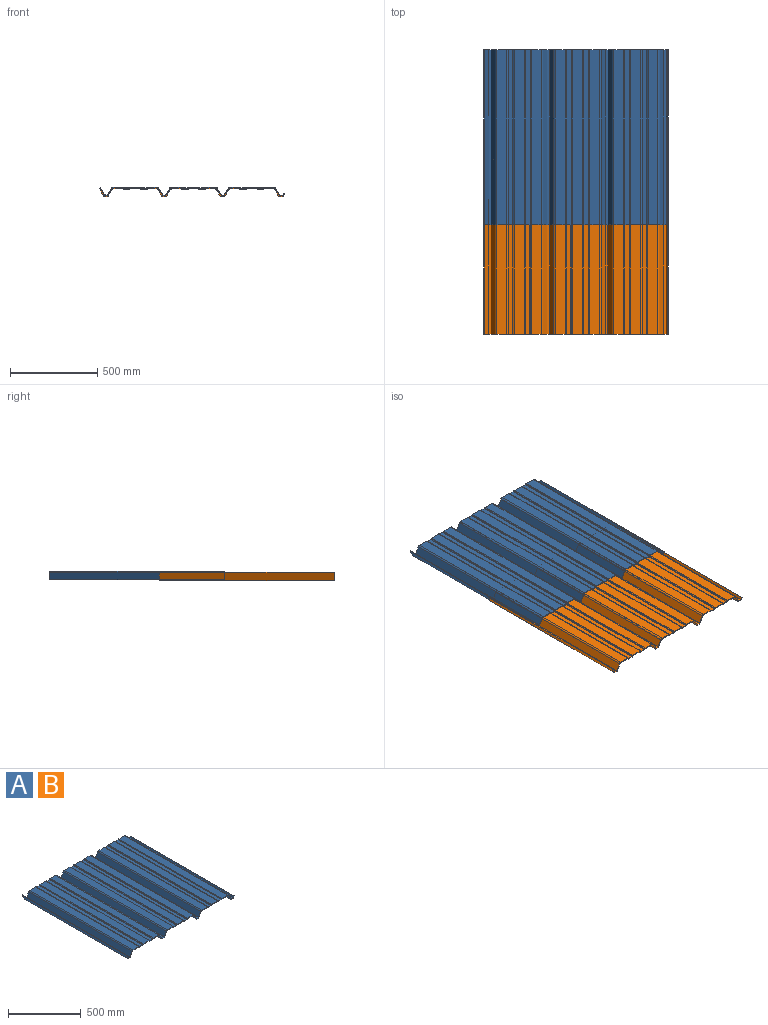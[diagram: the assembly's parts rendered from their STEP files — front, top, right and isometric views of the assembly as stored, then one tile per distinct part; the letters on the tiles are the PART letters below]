
ASSEMBLY  parts=2 mates=1
PART A: 157 faces, bbox 1056.4x1000x50 mm
  f0: plane 1000x41mm, normal (-0.87,0,-0.5), area 47365.7mm2, adj f1,f154,f155,f156
  f1: cylinder r=6mm len=1000mm, axis (0,1,0), area 6279mm2, adj f0,f2,f155,f156
  f2: plane 1000x15.07mm, normal (0,0,-1), area 15074.6mm2, adj f1,f3,f155,f156
  f3: cylinder r=6mm len=1000mm, axis (0,1,0), area 6283.2mm2, adj f2,f4,f155,f156
  f4: plane 1000x38mm, normal (0.87,0,-0.5), area 43878.6mm2, adj f3,f5,f155,f156
  f5: cylinder r=6mm len=1000mm, axis (0,1,0), area 6283.2mm2, adj f4,f6,f155,f156
  f6: plane 1000x57.03mm, normal (0,0,-1), area 57032.5mm2, adj f5,f7,f155,f156
  f7: cylinder r=1.7mm len=1000mm, axis (0,1,0), area 1276.9mm2, adj f6,f8,f155,f156
  f8: plane 1000x3.84mm, normal (-0.68,0,-0.73), area 5253.3mm2, adj f7,f9,f155,f156
  f9: cylinder r=1.7mm len=1000mm, axis (0,1,0), area 1276.9mm2, adj f8,f10,f155,f156
  f10: plane 1000x28.68mm, normal (0,0,-1), area 28679.7mm2, adj f9,f11,f155,f156
  f11: cylinder r=1.7mm len=1000mm, axis (0,1,0), area 1276.9mm2, adj f10,f12,f155,f156
  f12: plane 1000x3.84mm, normal (0.68,0,-0.73), area 5253.4mm2, adj f11,f13,f155,f156
  f13: cylinder r=1.7mm len=1000mm, axis (0,1,0), area 1276.9mm2, adj f12,f14,f155,f156
  f14: plane 1000x58mm, normal (0,0,-1), area 58000mm2, adj f13,f15,f155,f156
  f15: cylinder r=1.7mm len=1000mm, axis (0,1,0), area 1276.9mm2, adj f14,f16,f155,f156
  f16: plane 1000x3.84mm, normal (-0.68,0,-0.73), area 5253.3mm2, adj f15,f17,f155,f156
  f17: cylinder r=1.7mm len=1000mm, axis (0,1,0), area 1276.9mm2, adj f16,f18,f155,f156
  f18: plane 1000x28.68mm, normal (0,0,-1), area 28679.7mm2, adj f17,f19,f155,f156
  f19: cylinder r=1.7mm len=1000mm, axis (0,1,0), area 1276.9mm2, adj f18,f20,f155,f156
  f20: plane 1000x3.84mm, normal (0.68,0,-0.73), area 5253.4mm2, adj f19,f21,f155,f156
  f21: cylinder r=1.7mm len=1000mm, axis (0,1,0), area 1276.9mm2, adj f20,f22,f155,f156
  f22: plane 1000x55.54mm, normal (0,0,-1), area 55537.2mm2, adj f21,f23,f155,f156
  f23: cylinder r=6mm len=1000mm, axis (0,1,0), area 6281.3mm2, adj f22,f24,f155,f156
  f24: plane 1000x39mm, normal (-0.87,0,-0.5), area 45045.5mm2, adj f23,f25,f155,f156
  f25: cylinder r=6mm len=1000mm, axis (0,1,0), area 6281.3mm2, adj f24,f26,f155,f156
  f26: plane 1000x16.07mm, normal (0,0,-1), area 16074.4mm2, adj f25,f27,f155,f156
  f27: cylinder r=6mm len=1000mm, axis (0,1,0), area 6281.3mm2, adj f26,f28,f155,f156
  f28: plane 1000x39mm, normal (0.87,0,-0.5), area 45045.5mm2, adj f27,f29,f155,f156
  f29: cylinder r=6mm len=1000mm, axis (0,1,0), area 6281.3mm2, adj f28,f30,f155,f156
  f30: plane 1000x55.54mm, normal (0,0,-1), area 55537.2mm2, adj f29,f31,f155,f156
  f31: cylinder r=1.7mm len=1000mm, axis (0,1,0), area 1276.9mm2, adj f30,f32,f155,f156
  f32: plane 1000x3.84mm, normal (-0.68,0,-0.73), area 5253.3mm2, adj f31,f33,f155,f156
  f33: cylinder r=1.7mm len=1000mm, axis (0,1,0), area 1276.9mm2, adj f32,f34,f155,f156
  f34: plane 1000x28.68mm, normal (0,0,-1), area 28679.7mm2, adj f33,f35,f155,f156
  f35: cylinder r=1.7mm len=1000mm, axis (0,1,0), area 1276.9mm2, adj f34,f36,f155,f156
  f36: plane 1000x3.84mm, normal (0.68,0,-0.73), area 5253.4mm2, adj f35,f37,f155,f156
  f37: cylinder r=1.7mm len=1000mm, axis (0,1,0), area 1276.9mm2, adj f36,f38,f155,f156
  f38: plane 1000x58.3mm, normal (0,0,-1), area 58300mm2, adj f37,f39,f155,f156
  f39: cylinder r=1.7mm len=1000mm, axis (0,1,0), area 1276.9mm2, adj f38,f40,f155,f156
  f40: plane 1000x3.84mm, normal (-0.68,0,-0.73), area 5253.3mm2, adj f39,f41,f155,f156
  f41: cylinder r=1.7mm len=1000mm, axis (0,1,0), area 1276.9mm2, adj f40,f42,f155,f156
  f42: plane 1000x28.68mm, normal (0,0,-1), area 28679.7mm2, adj f41,f43,f155,f156
  f43: cylinder r=1.7mm len=1000mm, axis (0,1,0), area 1276.9mm2, adj f42,f44,f155,f156
  f44: plane 1000x3.84mm, normal (0.68,0,-0.73), area 5253.4mm2, adj f43,f45,f155,f156
  f45: cylinder r=1.7mm len=1000mm, axis (0,1,0), area 1276.9mm2, adj f44,f46,f155,f156
  f46: plane 1000x55.54mm, normal (0,0,-1), area 55537.2mm2, adj f45,f47,f155,f156
  f47: cylinder r=6mm len=1000mm, axis (0,1,0), area 6281.3mm2, adj f46,f48,f155,f156
  f48: plane 1000x39mm, normal (-0.87,0,-0.5), area 45045.5mm2, adj f47,f49,f155,f156
  f49: cylinder r=6mm len=1000mm, axis (0,1,0), area 6281.3mm2, adj f48,f50,f155,f156
  f50: plane 1000x16.07mm, normal (0,0,-1), area 16074.4mm2, adj f49,f51,f155,f156
  f51: cylinder r=6mm len=1000mm, axis (0,1,0), area 6281.3mm2, adj f50,f52,f155,f156
  f52: plane 1000x39mm, normal (0.87,0,-0.5), area 45045.5mm2, adj f51,f53,f155,f156
  f53: cylinder r=6mm len=1000mm, axis (0,1,0), area 6281.3mm2, adj f52,f54,f155,f156
  f54: plane 1000x55.54mm, normal (0,0,-1), area 55537.2mm2, adj f53,f55,f155,f156
  f55: cylinder r=1.7mm len=1000mm, axis (0,1,0), area 1276.9mm2, adj f54,f56,f155,f156
  f56: plane 1000x3.84mm, normal (-0.68,0,-0.73), area 5253.3mm2, adj f55,f57,f155,f156
  f57: cylinder r=1.7mm len=1000mm, axis (0,1,0), area 1276.9mm2, adj f56,f58,f155,f156
  f58: plane 1000x28.68mm, normal (0,0,-1), area 28679.7mm2, adj f57,f59,f155,f156
  f59: cylinder r=1.7mm len=1000mm, axis (0,1,0), area 1276.9mm2, adj f58,f60,f155,f156
  f60: plane 1000x3.84mm, normal (0.68,0,-0.73), area 5253.4mm2, adj f59,f61,f155,f156
  f61: cylinder r=1.7mm len=1000mm, axis (0,1,0), area 1276.9mm2, adj f60,f62,f155,f156
  f62: plane 1000x58.3mm, normal (0,0,-1), area 58300mm2, adj f61,f63,f155,f156
  f63: cylinder r=1.7mm len=1000mm, axis (0,1,0), area 1276.9mm2, adj f62,f64,f155,f156
  f64: plane 1000x3.84mm, normal (-0.68,0,-0.73), area 5253.3mm2, adj f63,f65,f155,f156
  f65: cylinder r=1.7mm len=1000mm, axis (0,1,0), area 1276.9mm2, adj f64,f66,f155,f156
  f66: plane 1000x28.69mm, normal (0,0,-1), area 28687.2mm2, adj f65,f67,f155,f156
  f67: cylinder r=1.7mm len=1000mm, axis (0,1,0), area 1266.5mm2, adj f66,f68,f155,f156
  f68: plane 1000x3.94mm, normal (0.68,0,-0.74), area 5362.6mm2, adj f67,f69,f155,f156
  f69: cylinder r=1.7mm len=1000mm, axis (0,1,0), area 1172mm2, adj f68,f70,f155,f156
  f70: plane 1000x56.52mm, normal (0,0,-1), area 56524.1mm2, adj f69,f71,f155,f156
  f71: cylinder r=6mm len=1000mm, axis (0,1,0), area 6384.5mm2, adj f70,f72,f155,f156
  f72: plane 1000x38.82mm, normal (-0.87,0,-0.48), area 44384.7mm2, adj f71,f73,f155,f156
  f73: cylinder r=6mm len=1000mm, axis (0,1,0), area 6387.9mm2, adj f72,f74,f155,f156
  f74: plane 1000x16.64mm, normal (0,0,-1), area 16636.9mm2, adj f73,f75,f155,f156
  f75: cylinder r=5mm len=1000mm, axis (0,1,0), area 5148.7mm2, adj f74,f76,f155,f156
  f76: plane 1000x11.69mm, normal (0.86,0,-0.52), area 13632.1mm2, adj f75,f77,f155,f156
  f77: plane 1000x4.29mm, normal (0.52,0,0.86), area 5000mm2, adj f76,f78,f155,f156
  f78: plane 1000x11.69mm, normal (-0.86,0,0.52), area 13632.1mm2, adj f77,f79,f155,f156
  f79: plane 1000x16.64mm, normal (0,0,1), area 16636.9mm2, adj f78,f80,f155,f156
  f80: cylinder r=1mm len=1000mm, axis (0,1,0), area 1064.7mm2, adj f79,f81,f155,f156
  f81: plane 1000x38.82mm, normal (0.87,0,0.48), area 44384.7mm2, adj f80,f82,f155,f156
  f82: cylinder r=11mm len=1000mm, axis (0,1,0), area 11704.9mm2, adj f81,f83,f155,f156
  f83: plane 1000x56.62mm, normal (0,0,1), area 56618.2mm2, adj f82,f84,f155,f156
  f84: cylinder r=6.7mm len=1000mm, axis (0,1,0), area 4805.9mm2, adj f83,f85,f155,f156
  f85: plane 1000x2.71mm, normal (-0.68,0,0.74), area 3682.3mm2, adj f84,f86,f155,f156
  f86: cylinder r=1mm len=1000mm, axis (0,1,0), area 745mm2, adj f85,f87,f155,f156
  f87: plane 1000x25.31mm, normal (0,0,1), area 25311.6mm2, adj f86,f88,f155,f156
  f88: cylinder r=1mm len=1000mm, axis (0,1,0), area 751.1mm2, adj f87,f89,f155,f156
  f89: plane 1000x2.6mm, normal (0.68,0,0.73), area 3558mm2, adj f88,f90,f155,f156
  f90: cylinder r=6.7mm len=1000mm, axis (0,1,0), area 5032.5mm2, adj f89,f91,f155,f156
  f91: plane 1000x58.3mm, normal (0,0,1), area 58300mm2, adj f90,f92,f155,f156
  f92: cylinder r=6.7mm len=1000mm, axis (0,1,0), area 5032.5mm2, adj f91,f93,f155,f156
  f93: plane 1000x2.6mm, normal (-0.68,0,0.73), area 3558mm2, adj f92,f94,f155,f156
  f94: cylinder r=1mm len=1000mm, axis (0,1,0), area 751.1mm2, adj f93,f95,f155,f156
  f95: plane 1000x25.29mm, normal (0,0,1), area 25288.9mm2, adj f94,f96,f155,f156
  f96: cylinder r=1mm len=1000mm, axis (0,1,0), area 751.1mm2, adj f95,f97,f155,f156
  f97: plane 1000x2.6mm, normal (0.68,0,0.73), area 3558mm2, adj f96,f98,f155,f156
  f98: cylinder r=6.7mm len=1000mm, axis (0,1,0), area 5032.5mm2, adj f97,f99,f155,f156
  f99: plane 1000x55.54mm, normal (0,0,1), area 55537.2mm2, adj f98,f100,f155,f156
  f100: cylinder r=11mm len=1000mm, axis (0,1,0), area 11515.6mm2, adj f99,f101,f155,f156
  f101: plane 1000x39mm, normal (-0.87,0,0.5), area 45045.5mm2, adj f100,f102,f155,f156
  f102: cylinder r=1mm len=1000mm, axis (0,1,0), area 1046.9mm2, adj f101,f103,f155,f156
  f103: plane 1000x16.07mm, normal (0,0,1), area 16074.4mm2, adj f102,f104,f155,f156
  f104: cylinder r=1mm len=1000mm, axis (0,1,0), area 1046.9mm2, adj f103,f105,f155,f156
  f105: plane 1000x39mm, normal (0.87,0,0.5), area 45045.5mm2, adj f104,f106,f155,f156
  f106: cylinder r=11mm len=1000mm, axis (0,1,0), area 11515.6mm2, adj f105,f107,f155,f156
  f107: plane 1000x55.54mm, normal (0,0,1), area 55537.2mm2, adj f106,f108,f155,f156
  f108: cylinder r=6.7mm len=1000mm, axis (0,1,0), area 5032.5mm2, adj f107,f109,f155,f156
  f109: plane 1000x2.6mm, normal (-0.68,0,0.73), area 3558mm2, adj f108,f110,f155,f156
  f110: cylinder r=1mm len=1000mm, axis (0,1,0), area 751.1mm2, adj f109,f111,f155,f156
  f111: plane 1000x25.29mm, normal (0,0,1), area 25288.9mm2, adj f110,f112,f155,f156
  f112: cylinder r=1mm len=1000mm, axis (0,1,0), area 751.1mm2, adj f111,f113,f155,f156
  f113: plane 1000x2.6mm, normal (0.68,0,0.73), area 3558mm2, adj f112,f114,f155,f156
  f114: cylinder r=6.7mm len=1000mm, axis (0,1,0), area 5032.5mm2, adj f113,f115,f155,f156
  f115: plane 1000x58.3mm, normal (0,0,1), area 58300mm2, adj f114,f116,f155,f156
  f116: cylinder r=6.7mm len=1000mm, axis (0,1,0), area 5032.5mm2, adj f115,f117,f155,f156
  f117: plane 1000x2.6mm, normal (-0.68,0,0.73), area 3558mm2, adj f116,f118,f155,f156
  f118: cylinder r=1mm len=1000mm, axis (0,1,0), area 751.1mm2, adj f117,f119,f155,f156
  f119: plane 1000x25.29mm, normal (0,0,1), area 25288.9mm2, adj f118,f120,f155,f156
  f120: cylinder r=1mm len=1000mm, axis (0,1,0), area 751.1mm2, adj f119,f121,f155,f156
  f121: plane 1000x2.6mm, normal (0.68,0,0.73), area 3558mm2, adj f120,f122,f155,f156
  f122: cylinder r=6.7mm len=1000mm, axis (0,1,0), area 5032.5mm2, adj f121,f123,f155,f156
  f123: plane 1000x55.54mm, normal (0,0,1), area 55537.2mm2, adj f122,f124,f155,f156
  f124: cylinder r=11mm len=1000mm, axis (0,1,0), area 11515.6mm2, adj f123,f125,f155,f156
  f125: plane 1000x39mm, normal (-0.87,0,0.5), area 45045.5mm2, adj f124,f126,f155,f156
  f126: cylinder r=1mm len=1000mm, axis (0,1,0), area 1046.9mm2, adj f125,f127,f155,f156
  f127: plane 1000x16.07mm, normal (0,0,1), area 16074.4mm2, adj f126,f128,f155,f156
  f128: cylinder r=1mm len=1000mm, axis (0,1,0), area 1046.9mm2, adj f127,f129,f155,f156
  f129: plane 1000x39mm, normal (0.87,0,0.5), area 45045.5mm2, adj f128,f130,f155,f156
  f130: cylinder r=11mm len=1000mm, axis (0,1,0), area 11515.6mm2, adj f129,f131,f155,f156
  f131: plane 1000x55.54mm, normal (0,0,1), area 55537.2mm2, adj f130,f132,f155,f156
  f132: cylinder r=6.7mm len=1000mm, axis (0,1,0), area 5032.5mm2, adj f131,f133,f155,f156
  f133: plane 1000x2.6mm, normal (-0.68,0,0.73), area 3558mm2, adj f132,f134,f155,f156
  f134: cylinder r=1mm len=1000mm, axis (0,1,0), area 751.1mm2, adj f133,f135,f155,f156
  f135: plane 1000x25.29mm, normal (0,0,1), area 25288.9mm2, adj f134,f136,f155,f156
  f136: cylinder r=1mm len=1000mm, axis (0,1,0), area 751.1mm2, adj f135,f137,f155,f156
  f137: plane 1000x2.6mm, normal (0.68,0,0.73), area 3558mm2, adj f136,f138,f155,f156
  f138: cylinder r=6.7mm len=1000mm, axis (0,1,0), area 5032.5mm2, adj f137,f139,f155,f156
  f139: plane 1000x58mm, normal (0,0,1), area 58000mm2, adj f138,f140,f155,f156
  f140: cylinder r=6.7mm len=1000mm, axis (0,1,0), area 5032.5mm2, adj f139,f141,f155,f156
  f141: plane 1000x2.6mm, normal (-0.68,0,0.73), area 3558mm2, adj f140,f142,f155,f156
  f142: cylinder r=1mm len=1000mm, axis (0,1,0), area 751.1mm2, adj f141,f143,f155,f156
  f143: plane 1000x25.29mm, normal (0,0,1), area 25288.9mm2, adj f142,f144,f155,f156
  f144: cylinder r=1mm len=1000mm, axis (0,1,0), area 751.1mm2, adj f143,f145,f155,f156
  f145: plane 1000x2.6mm, normal (0.68,0,0.73), area 3558mm2, adj f144,f146,f155,f156
  f146: cylinder r=6.7mm len=1000mm, axis (0,1,0), area 5032.5mm2, adj f145,f147,f155,f156
  f147: plane 1000x57.03mm, normal (0,0,1), area 57032.5mm2, adj f146,f148,f155,f156
  f148: cylinder r=11mm len=1000mm, axis (0,1,0), area 11519.2mm2, adj f147,f149,f155,f156
  f149: plane 1000x38mm, normal (-0.87,0,0.5), area 43878.6mm2, adj f148,f150,f155,f156
  f150: cylinder r=1mm len=1000mm, axis (0,1,0), area 1047.2mm2, adj f149,f151,f155,f156
  f151: plane 1000x15.07mm, normal (0,0,1), area 15074.6mm2, adj f150,f152,f155,f156
  f152: cylinder r=1mm len=1000mm, axis (0,1,0), area 1046.5mm2, adj f151,f153,f155,f156
  f153: plane 1000x41mm, normal (0.87,0,0.5), area 47365.5mm2, adj f152,f154,f155,f156
  f154: plane 1000x4.33mm, normal (-0.5,0,0.87), area 5000mm2, adj f0,f153,f155,f156
  f155: plane 1056.42x50.03mm, normal (0,-1,0), area 6253.8mm2, adj f0,f1,f2,f3,f4,f5,f6,f7
  f156: plane 1056.42x50.03mm, normal (0,1,0), area 6253.8mm2, adj f0,f1,f2,f3,f4,f5,f6,f7
PART B: same geometry as A
PLACE A t=(-373.5,306.23,100.15)mm
PLACE B t=(-373.94,-321.17,95.15)mm
MATE planar B.f83 <-> A.f70  axis (0,0,1) through (594.22,-821.17,100.17)mm
